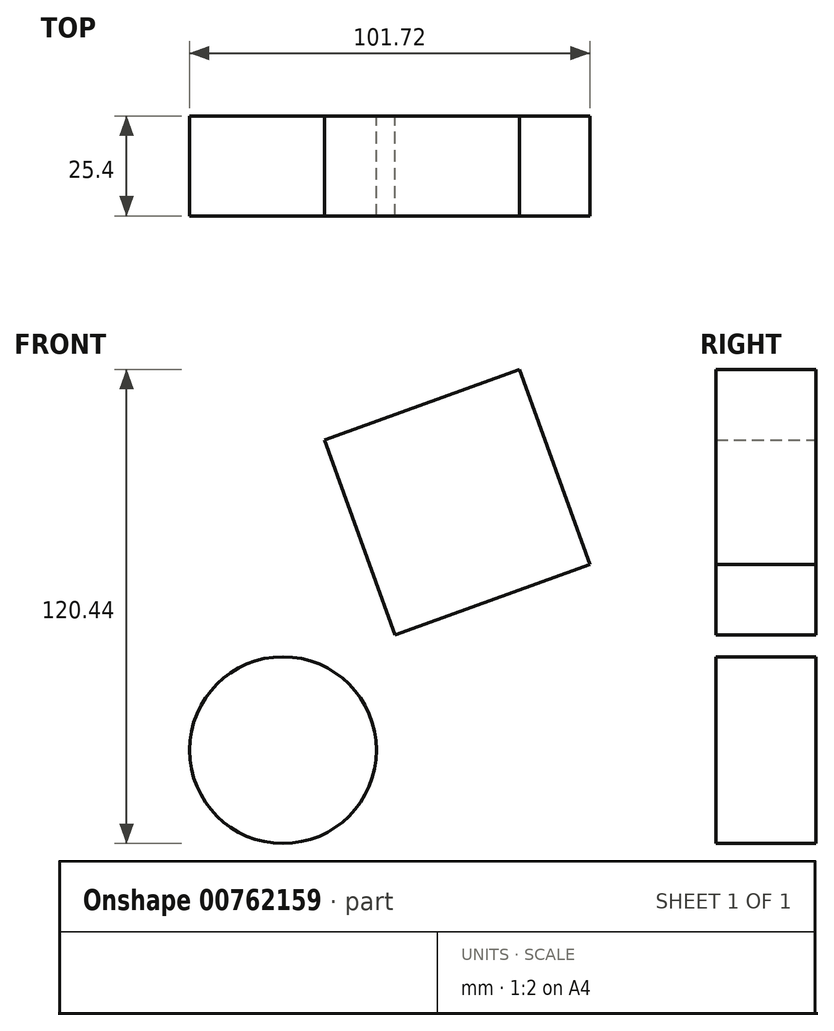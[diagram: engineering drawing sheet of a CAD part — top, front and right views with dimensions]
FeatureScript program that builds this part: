
annotation { "Feature Type Name" : "Feature", "Feature Type Description" : "" }
export const myFeature = defineFeature(function(context is Context, id is Id, definition is map)
    precondition{}
    {
        {
            var Q0;
            Q0=qCreatedBy(makeId("Front.planeOp"),FACE);
            var sketch = newSketch(context, id + "F0", { "sketchPlane" : qUnion([Q0])});
            skCircle(sketch, "E0", {"center": v(-7.34, -38.2) * mm, "radius": 23.73 * mm});
            skCircle(sketch, "E1.cCircle", {"center": v(36.92, 24.8) * mm, "radius": 26.35 * mm, "construction": true});
            skLineSegment(sketch, "E1.0", {"start": v(70.65, 8.94) * mm, "end": v(21.07, -8.94) * mm});
            skLineSegment(sketch, "E1.1", {"start": v(21.07, -8.94) * mm, "end": v(3.2, 40.64) * mm});
            skLineSegment(sketch, "E1.2", {"start": v(3.2, 40.64) * mm, "end": v(52.77, 58.52) * mm});
            skLineSegment(sketch, "E1.3", {"start": v(52.77, 58.52) * mm, "end": v(70.65, 8.94) * mm});
            skPoint(sketch, "E1.0.midPoint", {"position": v(45.86, 0) * mm});
            skSolve(sketch);
        }
        {
            var Q0;
            Q0 = qSketchRegion(id + "F0", true);
            extrude(context, id + "F1", {"entities" : qUnion([Q0]), "depth" : 25.4 * mm, "offsetDistance" : 25.4 * mm});
        }
    });
